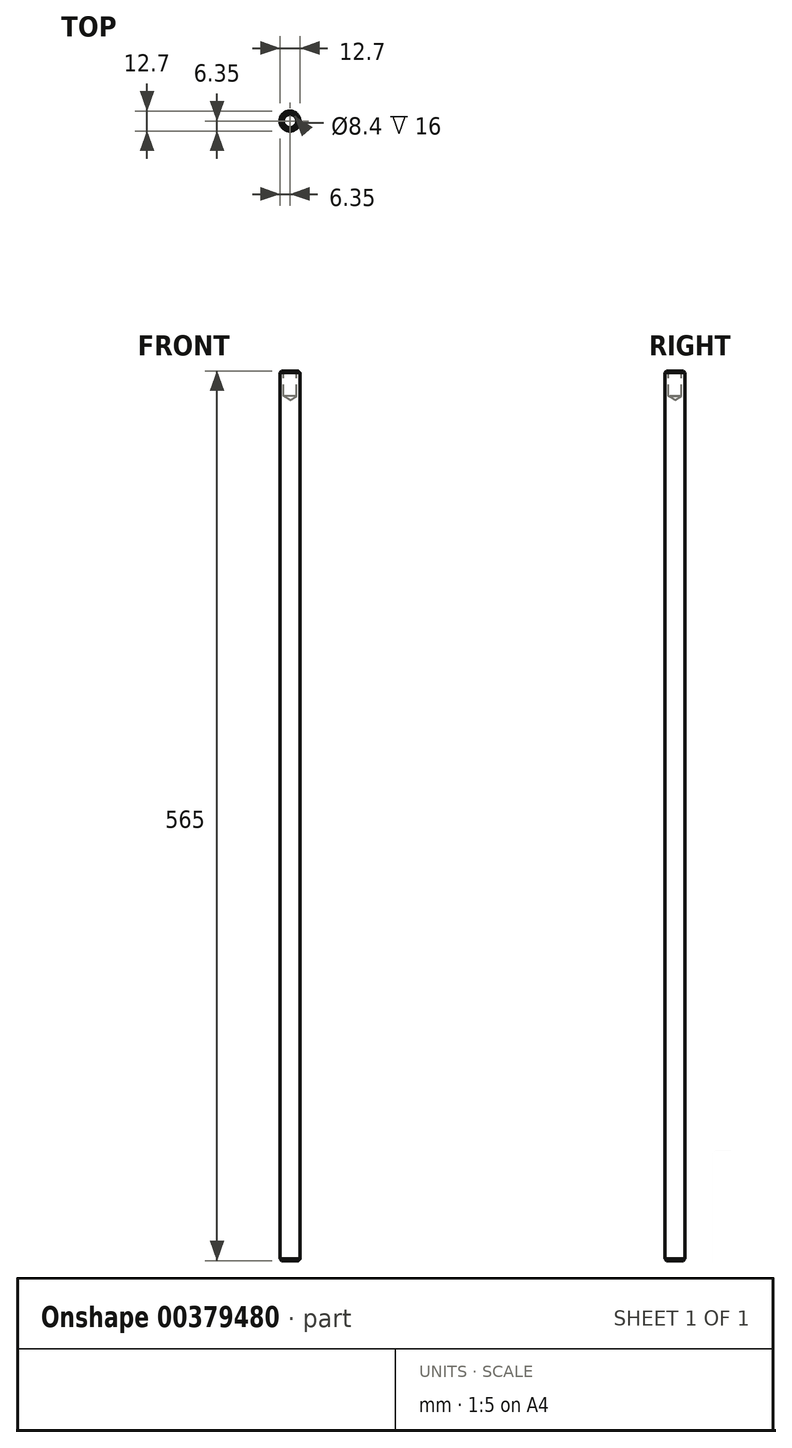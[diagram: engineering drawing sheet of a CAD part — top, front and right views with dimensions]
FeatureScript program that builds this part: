
annotation { "Feature Type Name" : "Feature", "Feature Type Description" : "" }
export const myFeature = defineFeature(function(context is Context, id is Id, definition is map)
    precondition{}
    {
        {
            var Q0;
            Q0=qCreatedBy(makeId("Top.planeOp"),FACE);
            var sketch = newSketch(context, id + "F0", { "sketchPlane" : qUnion([Q0])});
            skCircle(sketch, "E0", {"center": v(0, 0) * mm, "radius": 6.35 * mm});
            skSolve(sketch);
        }
        {
            var Q0;
            Q0=makeQuery(id+"F0.imprint","IMPRINT",FACE,{"disambiguationData":[TD([[makeQuery(id+"F0.imprint","IMPRINT",EDGE,{"derivedFrom":sQuery(id+"F0.wireOp",EDGE,"E0")}),1.0]])]});
            extrude(context, id + "F1", {"entities" : qUnion([Q0]), "endBound" : BoundingType.SYMMETRIC, "depth" : 565 * mm});
        }
        {
            var Q0;
            Q0=makeQuery(id+"F1.opExtrude","CAP_EDGE",EDGE,{"disambiguationData":[OSD([sQuery(id+"F0.wireOp",EDGE,"E0")])],"isStart":false});
            var Q1;
            Q1=makeQuery(id+"F1.opExtrude","CAP_EDGE",EDGE,{"disambiguationData":[OSD([sQuery(id+"F0.wireOp",EDGE,"E0")])],"isStart":true});
            chamfer(context, id + "F2", {"entities" : qUnion([Q0, Q1]), "chamferType" : ChamferType.OFFSET_ANGLE, "width" : 1.02 * mm, "oppositeDirection" : false, "angle" : 45 * degree, "tangentPropagation" : true});
        }
        {
            var Q0;
            Q0=makeQuery(id+"F1.opExtrude","CAP_FACE",FACE,{"disambiguationData":[OSD([sQuery(id+"F0.wireOp",EDGE,"E0")])],"isStart":false});
            var sketch = newSketch(context, id + "F3", { "sketchPlane" : qUnion([Q0])});
            skCircle(sketch, "E1.0.0", {"center": v(0, 0) * mm, "radius": 5.33 * mm});
            skSolve(sketch);
        }
        {
            var Q0;
            Q0=sQuery(id+"F3.wireOp",VERTEX,"E1.0.0.center");
            var Q1;
            Q1=makeQuery(id+"F1.opExtrude","SWEPT_BODY",BODY,{"disambiguationData":[OSD([sQuery(id+"F0.wireOp",EDGE,"E0")])]});
            hole(context, id + "F4", {"style" : HoleStyle.SIMPLE, "endStyle" : HoleEndStyle.BLIND, "standardTappedOrClearance" : lookupTablePath({ "standard" : "ISO", "fit" : "Close", "size" : "M8", "type" : "Clearance" }), "standardBlindInLast" : lookupTablePath({ "fit" : "Close", "standard" : "ISO", "size" : "M8", "type" : "Clearance" }), "holeDiameter" : 8.4 * mm, "holeDepth" : 16 * mm, "isTappedThrough" : true, "tappedDepth" : 12.7 * mm, "tapClearance" : 3, "locations" : qUnion([Q0]), "scope" : qUnion([Q1])});
        }
    });
